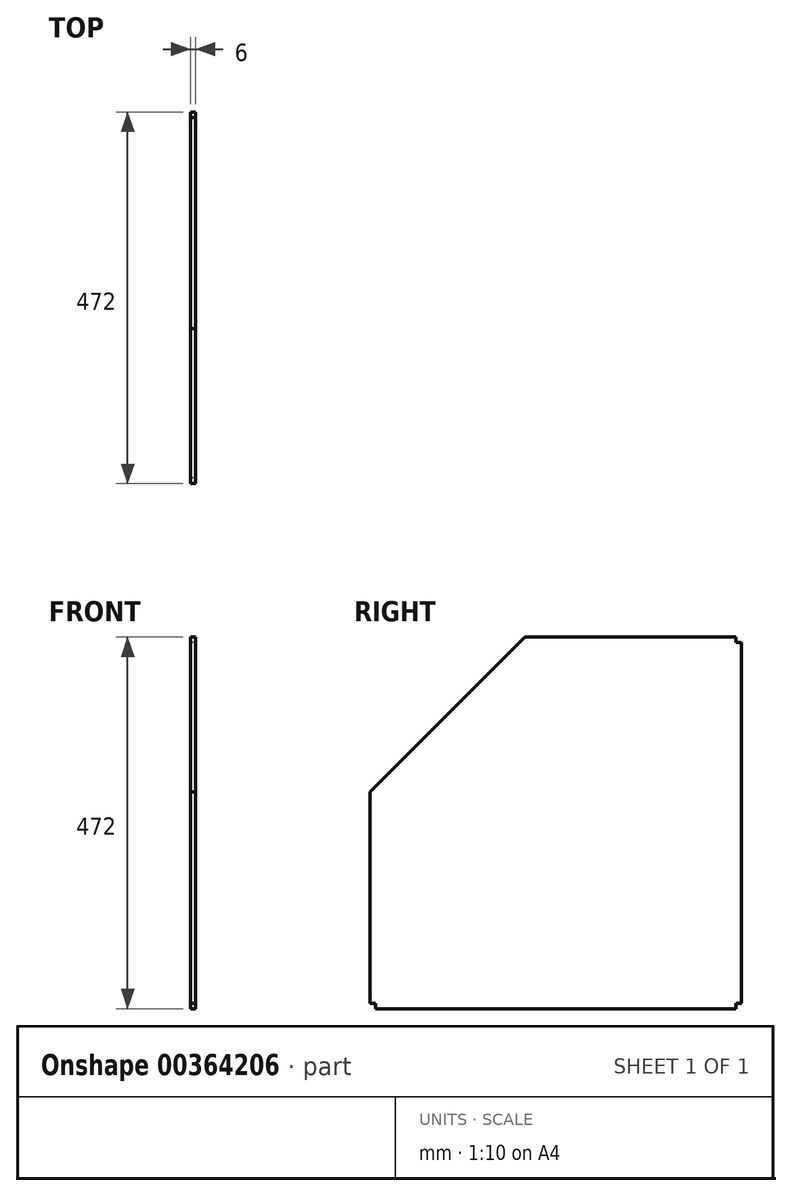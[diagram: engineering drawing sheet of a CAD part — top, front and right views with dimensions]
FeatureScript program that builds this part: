
annotation { "Feature Type Name" : "Feature", "Feature Type Description" : "" }
export const myFeature = defineFeature(function(context is Context, id is Id, definition is map)
    precondition{}
    {
        {
            var Q0;
            Q0=qCreatedBy(makeId("Right.planeOp"),FACE);
            var sketch = newSketch(context, id + "F0", { "sketchPlane" : qUnion([Q0])});
            skLineSegment(sketch, "E0.bottom", {"start": v(229, -236) * mm, "end": v(-229, -236) * mm});
            skLineSegment(sketch, "E0.top", {"start": v(229, 236) * mm, "end": v(-39.3, 236) * mm});
            skLineSegment(sketch, "E0.left", {"start": v(236, -229) * mm, "end": v(236, 229) * mm});
            skLineSegment(sketch, "E0.right", {"start": v(-236, -229) * mm, "end": v(-236, 39.3) * mm});
            skPoint(sketch, "E0.middle", {"position": v(0, 0) * mm});
            skPoint(sketch, "E1.orphan", {"position": v(-236, 236) * mm});
            skLineSegment(sketch, "E2", {"start": v(-236, 39.3) * mm, "end": v(-39.3, 236) * mm});
            skLineSegment(sketch, "E3.bottom", {"start": v(229, -229) * mm, "end": v(236, -229) * mm});
            skLineSegment(sketch, "E3.left", {"start": v(229, -229) * mm, "end": v(229, -236) * mm});
            skPoint(sketch, "E3.middle", {"position": v(236, -236) * mm});
            skLineSegment(sketch, "E4.bottom", {"start": v(236, 229) * mm, "end": v(229, 229) * mm});
            skLineSegment(sketch, "E4.right", {"start": v(229, 229) * mm, "end": v(229, 236) * mm});
            skPoint(sketch, "E4.middle", {"position": v(236, 236) * mm});
            skLineSegment(sketch, "E5.top", {"start": v(-229, -229) * mm, "end": v(-236, -229) * mm});
            skLineSegment(sketch, "E5.left", {"start": v(-229, -236) * mm, "end": v(-229, -229) * mm});
            skPoint(sketch, "E5.middle", {"position": v(-236, -236) * mm});
            skPoint(sketch, "E4.left.start.orphan", {"position": v(243, 229) * mm});
            skPoint(sketch, "E4.top.end.orphan", {"position": v(229, 243) * mm});
            skPoint(sketch, "E4.top.start.orphan", {"position": v(243, 243) * mm});
            skPoint(sketch, "E3.top.start.orphan", {"position": v(229, -243) * mm});
            skPoint(sketch, "E3.right.end.orphan", {"position": v(243, -243) * mm});
            skPoint(sketch, "E3.right.start.orphan", {"position": v(243, -229) * mm});
            skPoint(sketch, "E5.bottom.start.orphan", {"position": v(-229, -243) * mm});
            skPoint(sketch, "E5.right.end.orphan", {"position": v(-243, -229) * mm});
            skPoint(sketch, "E5.right.start.orphan", {"position": v(-243, -243) * mm});
            skSolve(sketch);
        }
        {
            var Q0;
            Q0=makeQuery(id+"F0.imprint","IMPRINT",FACE,{"disambiguationData":[TD([[makeQuery(id+"F0.imprint","IMPRINT",EDGE,{"derivedFrom":sQuery(id+"F0.wireOp",EDGE,"E0.bottom")}),-1.0]])]});
            extrude(context, id + "F1", {"entities" : qUnion([Q0]), "depth" : 6 * mm});
        }
    });
